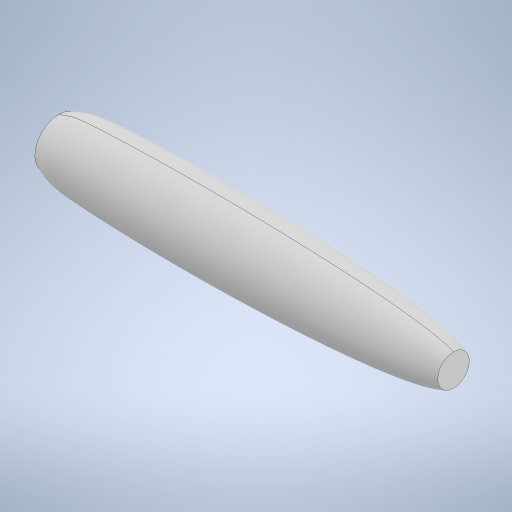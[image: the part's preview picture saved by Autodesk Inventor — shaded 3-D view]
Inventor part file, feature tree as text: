
AUTODESK INVENTOR PART (.ipt)
format: ipt  version: 2023 (Build 270158030, 158C)  size: 281,088 bytes
history: native  units: mm
features: revolve x1, sketch x1
ambient origin geometry x8: Origin, YZ Plane, XZ Plane, XY Plane, X Axis, Y Axis, Z Axis, Center Point
bodies: Solid1 (feature_tree)
feature tree (2):
  revolve  "Revolution1"  [1 undecoded]
  sketch  "Sketch3"  dims[d1=100.0mm d2=6.0mm d3=4.0mm d10=50.0mm d11=90.0deg]
note: 1 required parameter value undecoded (feature->parameter linkage not recoverable at this tier; creation-order binding heuristic only, values carry confidence <= 0.55)
